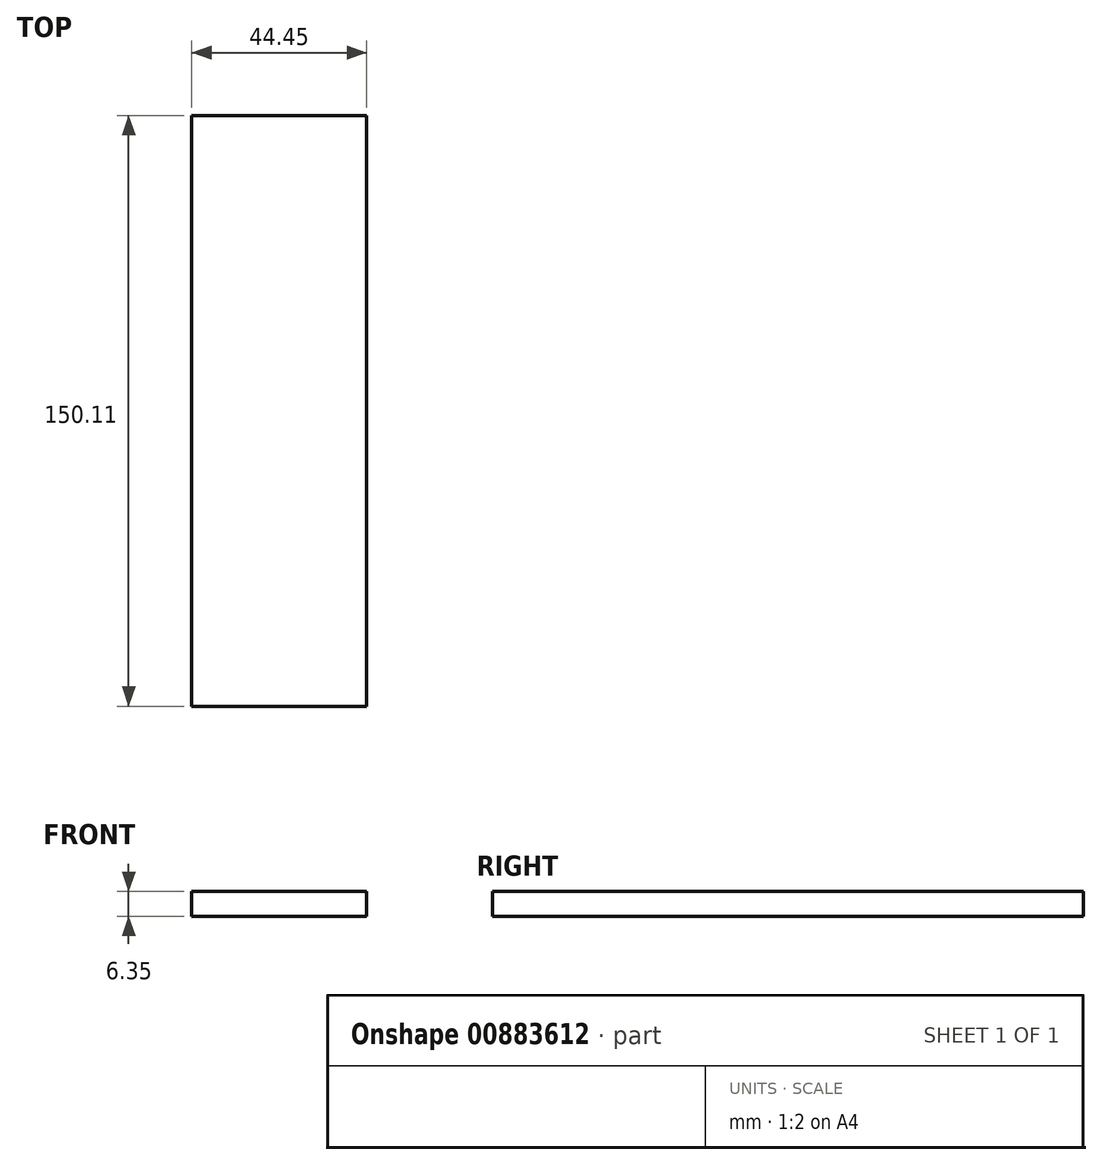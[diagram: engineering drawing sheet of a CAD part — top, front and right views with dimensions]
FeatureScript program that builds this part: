
annotation { "Feature Type Name" : "Feature", "Feature Type Description" : "" }
export const myFeature = defineFeature(function(context is Context, id is Id, definition is map)
    precondition{}
    {
        {
            var Q0;
            Q0=qCreatedBy(makeId("Top.planeOp"),FACE);
            var sketch = newSketch(context, id + "F0", { "sketchPlane" : qUnion([Q0])});
            skLineSegment(sketch, "E0.bottom", {"start": v(0, 0) * mm, "end": v(44.45, 0) * mm});
            skLineSegment(sketch, "E0.top", {"start": v(0, -150.11) * mm, "end": v(44.45, -150.11) * mm});
            skLineSegment(sketch, "E0.left", {"start": v(0, 0) * mm, "end": v(0, -150.11) * mm});
            skLineSegment(sketch, "E0.right", {"start": v(44.45, 0) * mm, "end": v(44.45, -150.11) * mm});
            skSolve(sketch);
        }
        {
            var Q0;
            Q0=makeQuery(id+"F0.imprint","IMPRINT",FACE,{"disambiguationData":[TD([[makeQuery(id+"F0.imprint","IMPRINT",EDGE,{"derivedFrom":sQuery(id+"F0.wireOp",EDGE,"E0.bottom")}),-1.0]])]});
            extrude(context, id + "F1", {"entities" : qUnion([Q0]), "depth" : 6.35 * mm, "offsetDistance" : 25.4 * mm});
        }
    });
